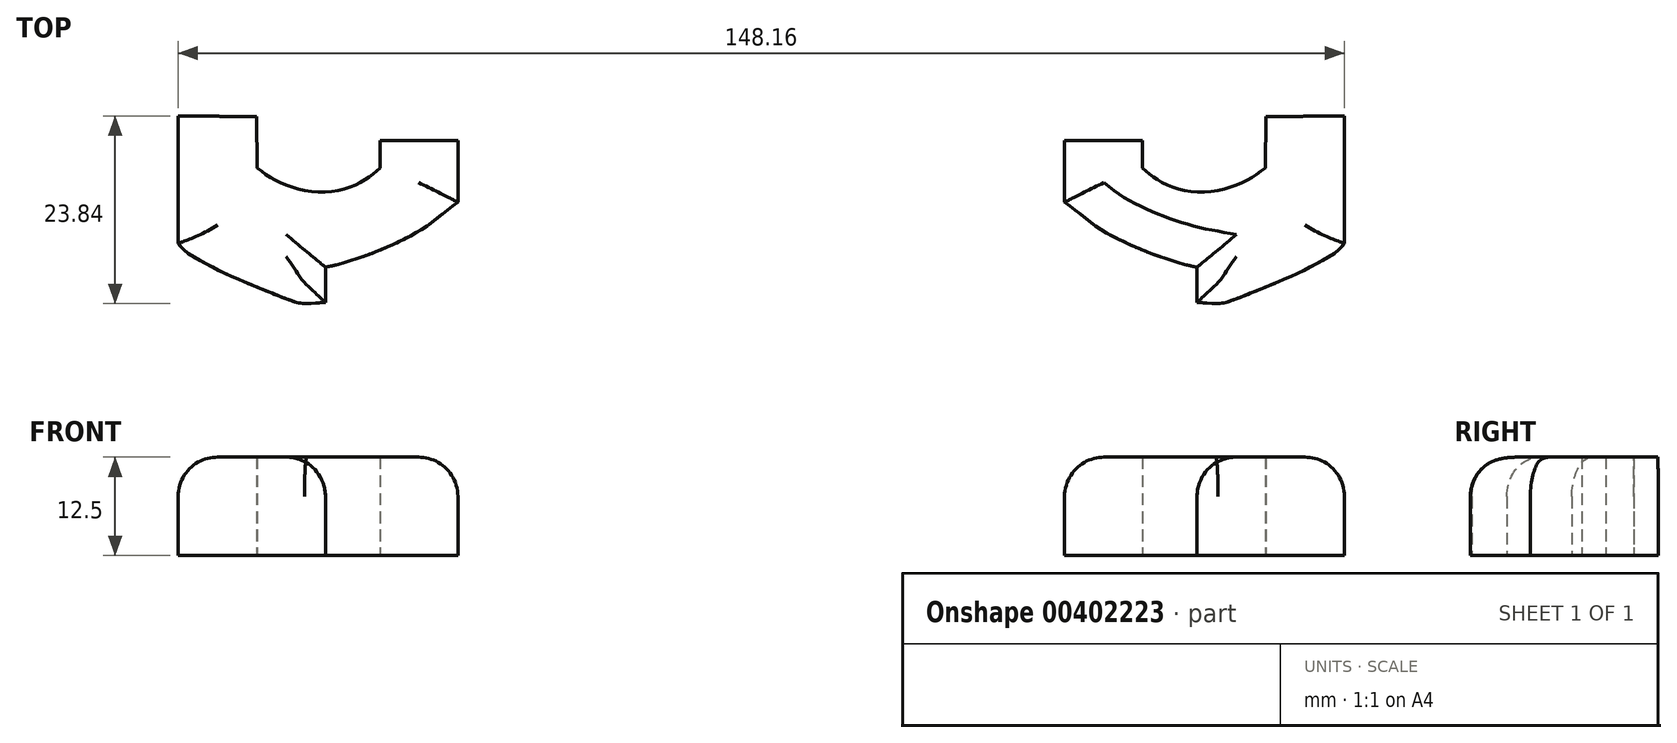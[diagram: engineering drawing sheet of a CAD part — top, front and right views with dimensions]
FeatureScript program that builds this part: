
annotation { "Feature Type Name" : "Feature", "Feature Type Description" : "" }
export const myFeature = defineFeature(function(context is Context, id is Id, definition is map)
    precondition{}
    {
        {
            var Q0;
            Q0=qCreatedBy(makeId("Top.planeOp"),FACE);
            var sketch = newSketch(context, id + "F0", { "sketchPlane" : qUnion([Q0])});
            skLineSegment(sketch, "E0", {"start": v(104.21, 74.07) * mm, "end": v(154.21, 74.07) * mm, "construction": true});
            skFitSpline(sketch, "E1", {"points": [v(122.06, 67.61) * mm, v(112.09, 67.7) * mm], "startDerivative": vector(-15.2, 0.08) * mm, "endDerivative": vector(-15.2, 0.08) * mm});
            skFitSpline(sketch, "E2", {"points": [v(112.09, 67.7) * mm, v(112.09, 51.47) * mm], "startDerivative": vector(0, -17.12) * mm, "endDerivative": vector(0, -17.12) * mm});
            skFitSpline(sketch, "E3", {"points": [v(112.09, 51.47) * mm, v(114.47, 49.57) * mm, v(118.11, 47.67) * mm, v(124.94, 44.81) * mm, v(128.1, 43.86) * mm, v(130.81, 44.02) * mm], "startDerivative": vector(17.57, -20.2) * mm, "endDerivative": vector(13.64, 0.61) * mm});
            skFitSpline(sketch, "E4", {"points": [v(130.81, 44.02) * mm, v(130.81, 48.48) * mm], "startDerivative": vector(0, 10.24) * mm, "endDerivative": vector(0, 10.24) * mm});
            skFitSpline(sketch, "E5", {"points": [v(130.81, 48.48) * mm, v(134.4, 49.44) * mm, v(138.83, 51.12) * mm, v(143.77, 53.76) * mm, v(147.64, 56.73) * mm], "startDerivative": vector(16.81, 3.27) * mm, "endDerivative": vector(22.51, 15.42) * mm});
            skFitSpline(sketch, "E6", {"points": [v(147.64, 56.73) * mm, v(147.64, 64.59) * mm], "startDerivative": vector(0, 11.16) * mm, "endDerivative": vector(0, 11.16) * mm});
            skFitSpline(sketch, "E7", {"points": [v(147.64, 64.59) * mm, v(137.76, 64.59) * mm], "startDerivative": vector(-13.76, 0) * mm, "endDerivative": vector(-13.76, 0) * mm});
            skFitSpline(sketch, "E8", {"points": [v(137.76, 64.59) * mm, v(137.76, 61.06) * mm], "startDerivative": vector(0, -3.53) * mm, "endDerivative": vector(0, -3.53) * mm});
            skFitSpline(sketch, "E9", {"points": [v(137.76, 61.06) * mm, v(135.33, 59.3) * mm, v(130.81, 58.04) * mm, v(125.42, 59.05) * mm, v(122.15, 61.06) * mm], "startDerivative": vector(-10.47, -8.75) * mm, "endDerivative": vector(-12.29, 9.13) * mm});
            skFitSpline(sketch, "E10", {"points": [v(122.15, 61.06) * mm, v(122.06, 67.61) * mm], "startDerivative": vector(-0.08, 6.55) * mm, "endDerivative": vector(-0.08, 6.55) * mm});
            skLineSegment(sketch, "E11", {"start": v(186.17, 56.73) * mm, "end": v(186.17, 160.4) * mm, "construction": true});
            skLineSegment(sketch, "E12", {"start": v(186.17, 160.4) * mm, "end": v(186.17, 32.6) * mm, "construction": true});
            skFitSpline(sketch, "E13.MirrorCS", {"points": [v(241.52, 48.48) * mm, v(237.93, 49.44) * mm, v(233.5, 51.12) * mm, v(228.57, 53.76) * mm, v(224.7, 56.73) * mm], "startDerivative": vector(-16.81, 3.27) * mm, "endDerivative": vector(-22.51, 15.42) * mm});
            skFitSpline(sketch, "E14.MirrorCS", {"points": [v(224.7, 64.59) * mm, v(234.58, 64.59) * mm], "startDerivative": vector(13.76, 0) * mm, "endDerivative": vector(13.76, 0) * mm});
            skFitSpline(sketch, "E15.MirrorCS", {"points": [v(234.58, 61.06) * mm, v(237, 59.3) * mm, v(241.52, 58.04) * mm, v(246.91, 59.05) * mm, v(250.19, 61.06) * mm], "startDerivative": vector(10.47, -8.75) * mm, "endDerivative": vector(12.29, 9.13) * mm});
            skFitSpline(sketch, "E16.MirrorCS", {"points": [v(234.58, 64.59) * mm, v(234.58, 61.06) * mm], "startDerivative": vector(0, -3.53) * mm, "endDerivative": vector(0, -3.53) * mm});
            skFitSpline(sketch, "E17.MirrorCS", {"points": [v(250.19, 61.06) * mm, v(250.27, 67.61) * mm], "startDerivative": vector(0.08, 6.55) * mm, "endDerivative": vector(0.08, 6.55) * mm});
            skFitSpline(sketch, "E18.MirrorCS", {"points": [v(250.27, 67.61) * mm, v(260.25, 67.7) * mm], "startDerivative": vector(15.2, 0.08) * mm, "endDerivative": vector(15.2, 0.08) * mm});
            skFitSpline(sketch, "E19.MirrorCS", {"points": [v(260.25, 67.7) * mm, v(260.25, 51.47) * mm], "startDerivative": vector(0, -17.12) * mm, "endDerivative": vector(0, -17.12) * mm});
            skFitSpline(sketch, "E20.MirrorCS", {"points": [v(260.25, 51.47) * mm, v(257.87, 49.57) * mm, v(254.22, 47.67) * mm, v(247.4, 44.81) * mm, v(244.23, 43.86) * mm, v(241.52, 44.02) * mm], "startDerivative": vector(-17.57, -20.2) * mm, "endDerivative": vector(-13.64, 0.61) * mm});
            skFitSpline(sketch, "E21.MirrorCS", {"points": [v(241.52, 44.02) * mm, v(241.52, 48.48) * mm], "startDerivative": vector(0, 10.24) * mm, "endDerivative": vector(0, 10.24) * mm});
            skFitSpline(sketch, "E22.MirrorCS", {"points": [v(224.7, 56.73) * mm, v(224.7, 64.59) * mm], "startDerivative": vector(0, 11.16) * mm, "endDerivative": vector(0, 11.16) * mm});
            skSolve(sketch);
        }
        {
            var Q0;
            Q0 = qSketchRegion(id + "F0", true);
            extrude(context, id + "F1", {"entities" : qUnion([Q0]), "depth" : 12.5 * mm, "offsetDistance" : 25 * mm});
        }
        {
            var Q0;
            Q0=makeQuery(id+"F1.opExtrude","CAP_EDGE",EDGE,{"disambiguationData":[OSD([sQuery(id+"F0.wireOp",EDGE,"E2")])],"isStart":false});
            var Q1;
            Q1=makeQuery(id+"F1.opExtrude","CAP_EDGE",EDGE,{"disambiguationData":[OSD([sQuery(id+"F0.wireOp",EDGE,"E3")])],"isStart":false});
            var Q2;
            Q2=makeQuery(id+"F1.opExtrude","CAP_EDGE",EDGE,{"disambiguationData":[OSD([sQuery(id+"F0.wireOp",EDGE,"E4")])],"isStart":false});
            var Q3;
            Q3=makeQuery(id+"F1.opExtrude","CAP_EDGE",EDGE,{"disambiguationData":[OSD([sQuery(id+"F0.wireOp",EDGE,"E5")])],"isStart":false});
            var Q4;
            Q4=makeQuery(id+"F1.opExtrude","CAP_EDGE",EDGE,{"disambiguationData":[OSD([sQuery(id+"F0.wireOp",EDGE,"E6")])],"isStart":false});
            fillet(context, id + "F2", {"entities" : qUnion([Q0, Q1, Q2, Q3, Q4]), "radius" : 5 * mm, "tangentPropagation" : true, "allowEdgeOverflow" : false});
        }
        {
            var Q0;
            Q0=makeQuery(id+"F1.opExtrude","CAP_EDGE",EDGE,{"disambiguationData":[OSD([sQuery(id+"F0.wireOp",EDGE,"E13.MirrorCS")])],"isStart":false});
            var Q1;
            Q1=makeQuery(id+"F1.opExtrude","CAP_EDGE",EDGE,{"disambiguationData":[OSD([sQuery(id+"F0.wireOp",EDGE,"E22.MirrorCS")])],"isStart":false});
            var Q2;
            Q2=makeQuery(id+"F1.opExtrude","CAP_EDGE",EDGE,{"disambiguationData":[OSD([sQuery(id+"F0.wireOp",EDGE,"E21.MirrorCS")])],"isStart":false});
            var Q3;
            Q3=makeQuery(id+"F1.opExtrude","CAP_EDGE",EDGE,{"disambiguationData":[OSD([sQuery(id+"F0.wireOp",EDGE,"E20.MirrorCS")])],"isStart":false});
            var Q4;
            Q4=makeQuery(id+"F1.opExtrude","CAP_EDGE",EDGE,{"disambiguationData":[OSD([sQuery(id+"F0.wireOp",EDGE,"E19.MirrorCS")])],"isStart":false});
            fillet(context, id + "F3", {"entities" : qUnion([Q0, Q1, Q2, Q3, Q4]), "radius" : 5 * mm, "tangentPropagation" : true, "allowEdgeOverflow" : false});
        }
    });
